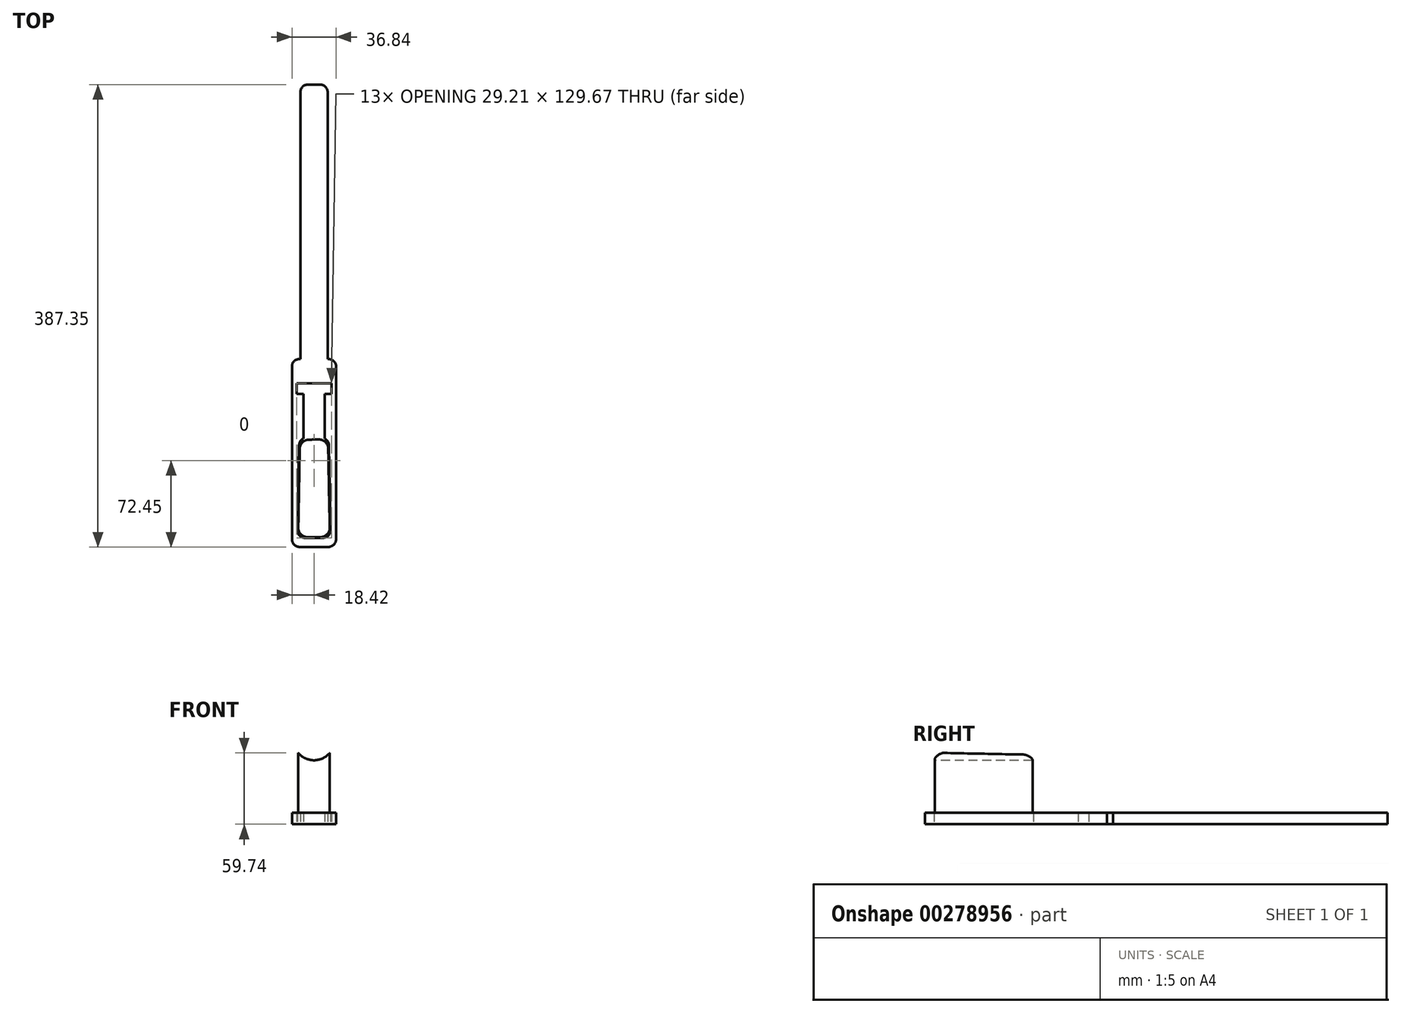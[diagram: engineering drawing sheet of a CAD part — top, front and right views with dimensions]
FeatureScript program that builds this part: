
annotation { "Feature Type Name" : "Feature", "Feature Type Description" : "" }
export const myFeature = defineFeature(function(context is Context, id is Id, definition is map)
    precondition{}
    {
        {
            var Q0;
            Q0=qCreatedBy(makeId("Top.planeOp"),FACE);
            var sketch = newSketch(context, id + "F0", { "sketchPlane" : qUnion([Q0])});
            skLineSegment(sketch, "E0", {"start": v(-18.42, 0) * mm, "end": v(-18.42, -85.1) * mm});
            skLineSegment(sketch, "E1", {"start": v(-12.07, -91.44) * mm, "end": v(12.07, -91.44) * mm});
            skLineSegment(sketch, "E2", {"start": v(18.42, -85.1) * mm, "end": v(18.42, 0) * mm});
            skLineSegment(sketch, "E3", {"start": v(-7.5, -83.82) * mm, "end": v(7.5, -83.82) * mm});
            skLineSegment(sketch, "E4", {"start": v(0, -112.75) * mm, "end": v(0, 326.55) * mm, "construction": true});
            skPoint(sketch, "E4.startSnap0", {"position": v(0, -91.44) * mm});
            skPoint(sketch, "E5", {"position": v(0, -83.82) * mm});
            skLineSegment(sketch, "E6", {"start": v(-18.42, 0) * mm, "end": v(-18.42, 60.96) * mm});
            skLineSegment(sketch, "E7", {"start": v(18.42, 0) * mm, "end": v(18.42, 60.96) * mm});
            skLineSegment(sketch, "E8", {"start": v(-8.9, 36.96) * mm, "end": v(-8.89, 0) * mm});
            skLineSegment(sketch, "E9", {"start": v(8.89, 36.96) * mm, "end": v(8.89, 0) * mm});
            skLineSegment(sketch, "E10", {"start": v(0, 0) * mm, "end": v(6.15, 0) * mm});
            skLineSegment(sketch, "E11", {"start": v(0, 0) * mm, "end": v(-6.15, 0) * mm});
            skLineSegment(sketch, "E12", {"start": v(-12.5, -6.23) * mm, "end": v(-13.85, -77.35) * mm});
            skLineSegment(sketch, "E13", {"start": v(12.5, -6.23) * mm, "end": v(13.85, -77.35) * mm});
            skPoint(sketch, "E14.visualSharp", {"position": v(-12.38, 0) * mm});
            skPoint(sketch, "E15.visualSharp", {"position": v(12.38, 0) * mm});
            skPoint(sketch, "E16.visualSharp", {"position": v(13.97, -83.82) * mm});
            skArc(sketch, "E16.filletArc", {"start": v(7.5, -83.82) * mm, "mid": v(12.03, -81.92) * mm, "end": v(13.85, -77.35) * mm});
            skPoint(sketch, "E17.visualSharp", {"position": v(-13.97, -83.82) * mm});
            skArc(sketch, "E17.filletArc", {"start": v(-13.85, -77.35) * mm, "mid": v(-12.03, -81.92) * mm, "end": v(-7.5, -83.82) * mm});
            skLineSegment(sketch, "E18", {"start": v(-8.89, 0) * mm, "end": v(-8.89, -0.62) * mm});
            skLineSegment(sketch, "E19", {"start": v(8.89, 0) * mm, "end": v(8.89, -0.62) * mm});
            skArc(sketch, "E20", {"start": v(12.5, -6.23) * mm, "mid": v(11.5, -2.91) * mm, "end": v(8.89, -0.62) * mm});
            skArc(sketch, "E21", {"start": v(-8.89, -0.62) * mm, "mid": v(-11.5, -2.91) * mm, "end": v(-12.5, -6.23) * mm});
            skLineSegment(sketch, "E22", {"start": v(0, 60.96) * mm, "end": v(11.43, 60.96) * mm});
            skLineSegment(sketch, "E23", {"start": v(0, 60.96) * mm, "end": v(-11.43, 60.96) * mm});
            skPoint(sketch, "E24", {"position": v(-18.42, 54.6) * mm});
            skPoint(sketch, "E25", {"position": v(18.42, 54.6) * mm});
            skLineSegment(sketch, "E26", {"start": v(-11.43, 60.96) * mm, "end": v(-11.43, 289.56) * mm});
            skLineSegment(sketch, "E27", {"start": v(-5.08, 295.91) * mm, "end": v(5.08, 295.91) * mm});
            skLineSegment(sketch, "E28", {"start": v(11.43, 289.56) * mm, "end": v(11.43, 60.96) * mm});
            skLineSegment(sketch, "E29", {"start": v(0, 60.96) * mm, "end": v(-12.07, 60.96) * mm});
            skLineSegment(sketch, "E30", {"start": v(0, 60.96) * mm, "end": v(12.07, 60.96) * mm});
            skArc(sketch, "E31", {"start": v(-12.07, 60.96) * mm, "mid": v(-16.56, 59.1) * mm, "end": v(-18.42, 54.6) * mm});
            skArc(sketch, "E32", {"start": v(18.42, 54.6) * mm, "mid": v(16.56, 59.1) * mm, "end": v(12.07, 60.96) * mm});
            skPoint(sketch, "E33.visualSharp", {"position": v(-11.43, 289.56) * mm});
            skArc(sketch, "E33.filletArc", {"start": v(-5.08, 295.91) * mm, "mid": v(-9.57, 294.05) * mm, "end": v(-11.43, 289.56) * mm});
            skPoint(sketch, "E34.visualSharp", {"position": v(11.43, 289.56) * mm});
            skArc(sketch, "E34.filletArc", {"start": v(11.43, 289.56) * mm, "mid": v(9.57, 294.05) * mm, "end": v(5.08, 295.91) * mm});
            skLineSegment(sketch, "E35", {"start": v(8.89, 36.96) * mm, "end": v(14.6, 36.96) * mm});
            skLineSegment(sketch, "E36", {"start": v(-8.9, 36.96) * mm, "end": v(-14.6, 36.96) * mm});
            skPoint(sketch, "E37.visualSharp", {"position": v(-18.42, -91.44) * mm});
            skArc(sketch, "E37.filletArc", {"start": v(-18.41, -85.1) * mm, "mid": v(-16.56, -89.58) * mm, "end": v(-12.07, -91.44) * mm});
            skPoint(sketch, "E38.visualSharp", {"position": v(18.42, -91.44) * mm});
            skArc(sketch, "E38.filletArc", {"start": v(12.07, -91.44) * mm, "mid": v(16.56, -89.58) * mm, "end": v(18.41, -85.1) * mm});
            skLineSegment(sketch, "E39", {"start": v(12.07, 66.04) * mm, "end": v(-12.07, 66.04) * mm});
            skArc(sketch, "E40", {"start": v(-12.07, 66.04) * mm, "mid": v(-16.13, 64.61) * mm, "end": v(-18.42, 60.96) * mm});
            skArc(sketch, "E41", {"start": v(18.42, 60.96) * mm, "mid": v(16.13, 64.61) * mm, "end": v(12.07, 66.04) * mm});
            skPoint(sketch, "E42", {"position": v(14.6, 45.85) * mm});
            skLineSegment(sketch, "E43", {"start": v(14.6, 36.96) * mm, "end": v(14.6, 45.85) * mm});
            skLineSegment(sketch, "E44", {"start": v(-14.6, 45.85) * mm, "end": v(-14.6, 36.96) * mm});
            skLineSegment(sketch, "E45", {"start": v(-14.6, 45.85) * mm, "end": v(14.6, 45.85) * mm});
            skSolve(sketch);
        }
        {
            var Q0;
            Q0 = qSketchRegion(id + "F0", true);
            extrude(context, id + "F1", {"entities" : qUnion([Q0]), "depth" : 9.52 * mm});
        }
        {
            var Q0;
            Q0=makeQuery(id+"F1.opExtrude","SWEPT_BODY",BODY,{"disambiguationData":[OSD([sQuery(id+"F0.wireOp",EDGE,"E0"),sQuery(id+"F0.wireOp",EDGE,"E1"),sQuery(id+"F0.wireOp",EDGE,"E2"),sQuery(id+"F0.wireOp",EDGE,"E3"),sQuery(id+"F0.wireOp",EDGE,"E6"),sQuery(id+"F0.wireOp",EDGE,"E7"),sQuery(id+"F0.wireOp",EDGE,"E8"),sQuery(id+"F0.wireOp",EDGE,"E9"),sQuery(id+"F0.wireOp",EDGE,"E12"),sQuery(id+"F0.wireOp",EDGE,"E13"),sQuery(id+"F0.wireOp",EDGE,"E16.filletArc"),sQuery(id+"F0.wireOp",EDGE,"E17.filletArc"),sQuery(id+"F0.wireOp",EDGE,"E18"),sQuery(id+"F0.wireOp",EDGE,"E19"),sQuery(id+"F0.wireOp",EDGE,"E20"),sQuery(id+"F0.wireOp",EDGE,"E21"),sQuery(id+"F0.wireOp",EDGE,"06W7z1AY-n0ql-A3Bi-P6vR-q7lxeoe17qw5"),sQuery(id+"F0.wireOp",EDGE,"bXarmPJa-DHQA-tuoh-5tIz-POXl1eP8OdJ6"),sQuery(id+"F0.wireOp",EDGE,"ymd9te90-yEeZ-0O9O-FOdn-OmkhNjDWxyUQ"),sQuery(id+"F0.wireOp",EDGE,"E26"),sQuery(id+"F0.wireOp",EDGE,"E27"),sQuery(id+"F0.wireOp",EDGE,"E28"),sQuery(id+"F0.wireOp",EDGE,"E33.filletArc"),sQuery(id+"F0.wireOp",EDGE,"E34.filletArc"),sQuery(id+"F0.wireOp",EDGE,"E35"),sQuery(id+"F0.wireOp",EDGE,"E36"),sQuery(id+"F0.wireOp",EDGE,"E37.filletArc"),sQuery(id+"F0.wireOp",EDGE,"E38.filletArc"),sQuery(id+"F0.wireOp",EDGE,"E39"),sQuery(id+"F0.wireOp",EDGE,"E40"),sQuery(id+"F0.wireOp",EDGE,"E41")])]});
            transform(context, id + "F2", {"entities" : qUnion([Q0]), "transformType" : TransformType.TRANSLATION_3D, "dx" : 0 * mm, "dy" : -113.28 * mm, "dz" : 0 * mm, "makeCopy" : false});
        }
        {
            var Q0;
            Q0=makeQuery(id+"F1.opExtrude","CAP_FACE",FACE,{"disambiguationData":[OSD([sQuery(id+"F0.wireOp",EDGE,"E0"),sQuery(id+"F0.wireOp",EDGE,"E1"),sQuery(id+"F0.wireOp",EDGE,"E2"),sQuery(id+"F0.wireOp",EDGE,"E3"),sQuery(id+"F0.wireOp",EDGE,"E6"),sQuery(id+"F0.wireOp",EDGE,"E7"),sQuery(id+"F0.wireOp",EDGE,"E8"),sQuery(id+"F0.wireOp",EDGE,"E9"),sQuery(id+"F0.wireOp",EDGE,"E12"),sQuery(id+"F0.wireOp",EDGE,"E13"),sQuery(id+"F0.wireOp",EDGE,"E16.filletArc"),sQuery(id+"F0.wireOp",EDGE,"E17.filletArc"),sQuery(id+"F0.wireOp",EDGE,"E18"),sQuery(id+"F0.wireOp",EDGE,"E19"),sQuery(id+"F0.wireOp",EDGE,"E20"),sQuery(id+"F0.wireOp",EDGE,"E21"),sQuery(id+"F0.wireOp",EDGE,"E26"),sQuery(id+"F0.wireOp",EDGE,"E27"),sQuery(id+"F0.wireOp",EDGE,"E28"),sQuery(id+"F0.wireOp",EDGE,"E33.filletArc"),sQuery(id+"F0.wireOp",EDGE,"E34.filletArc"),sQuery(id+"F0.wireOp",EDGE,"E35"),sQuery(id+"F0.wireOp",EDGE,"E36"),sQuery(id+"F0.wireOp",EDGE,"E37.filletArc"),sQuery(id+"F0.wireOp",EDGE,"E38.filletArc"),sQuery(id+"F0.wireOp",EDGE,"E39"),sQuery(id+"F0.wireOp",EDGE,"E40"),sQuery(id+"F0.wireOp",EDGE,"E41"),sQuery(id+"F0.wireOp",EDGE,"E43"),sQuery(id+"F0.wireOp",EDGE,"E44"),sQuery(id+"F0.wireOp",EDGE,"E45")])],"isStart":false});
            var sketch = newSketch(context, id + "F3", { "sketchPlane" : qUnion([Q0])});
            skArc(sketch, "E46", {"start": v(-12.07, -47.24) * mm, "mid": v(-16.13, -48.67) * mm, "end": v(-18.42, -52.32) * mm});
            skArc(sketch, "E47", {"start": v(18.42, -52.32) * mm, "mid": v(16.13, -48.67) * mm, "end": v(12.07, -47.24) * mm});
            skArc(sketch, "E48", {"start": v(12.07, -204.72) * mm, "mid": v(16.56, -202.86) * mm, "end": v(18.41, -198.37) * mm});
            skArc(sketch, "E49", {"start": v(7.5, -197.1) * mm, "mid": v(12.03, -195.2) * mm, "end": v(13.85, -190.63) * mm});
            skArc(sketch, "E50", {"start": v(-13.85, -190.63) * mm, "mid": v(-12.03, -195.2) * mm, "end": v(-7.5, -197.1) * mm});
            skArc(sketch, "E51", {"start": v(-18.41, -198.37) * mm, "mid": v(-16.56, -202.86) * mm, "end": v(-12.07, -204.72) * mm});
            skArc(sketch, "E52", {"start": v(-8.89, -113.9) * mm, "mid": v(-11.5, -116.2) * mm, "end": v(-12.5, -119.51) * mm});
            skArc(sketch, "E53", {"start": v(12.5, -119.51) * mm, "mid": v(11.5, -116.2) * mm, "end": v(8.89, -113.9) * mm});
            skArc(sketch, "E54", {"start": v(-5.08, 182.63) * mm, "mid": v(-9.57, 180.77) * mm, "end": v(-11.43, 176.28) * mm});
            skArc(sketch, "E55", {"start": v(11.43, 176.28) * mm, "mid": v(9.57, 180.77) * mm, "end": v(5.08, 182.63) * mm});
            skLineSegment(sketch, "E56", {"start": v(-5.08, 182.63) * mm, "end": v(5.08, 182.63) * mm});
            skLineSegment(sketch, "E57", {"start": v(-12.07, -47.24) * mm, "end": v(-11.43, -47.24) * mm});
            skLineSegment(sketch, "E58", {"start": v(-11.43, -47.24) * mm, "end": v(-11.43, 176.28) * mm});
            skLineSegment(sketch, "E59", {"start": v(11.43, 176.28) * mm, "end": v(11.43, -47.24) * mm});
            skLineSegment(sketch, "E60", {"start": v(11.43, -47.24) * mm, "end": v(12.07, -47.24) * mm});
            skLineSegment(sketch, "E61", {"start": v(-8.89, -113.9) * mm, "end": v(-8.89, -76.33) * mm});
            skLineSegment(sketch, "E62", {"start": v(-8.89, -76.33) * mm, "end": v(-14.6, -76.33) * mm});
            skLineSegment(sketch, "E63", {"start": v(-14.6, -76.33) * mm, "end": v(-14.6, -67.44) * mm});
            skLineSegment(sketch, "E64", {"start": v(-14.6, -67.44) * mm, "end": v(14.6, -67.44) * mm});
            skLineSegment(sketch, "E65", {"start": v(14.6, -67.44) * mm, "end": v(14.6, -76.33) * mm});
            skLineSegment(sketch, "E66", {"start": v(14.6, -76.33) * mm, "end": v(8.89, -76.33) * mm});
            skLineSegment(sketch, "E67", {"start": v(8.89, -76.33) * mm, "end": v(8.89, -113.9) * mm});
            skLineSegment(sketch, "E68", {"start": v(-13.85, -190.63) * mm, "end": v(-12.5, -119.51) * mm});
            skLineSegment(sketch, "E69", {"start": v(12.5, -119.51) * mm, "end": v(13.85, -190.63) * mm});
            skLineSegment(sketch, "E70", {"start": v(7.5, -197.1) * mm, "end": v(-7.5, -197.1) * mm});
            skLineSegment(sketch, "E71", {"start": v(-12.07, -204.72) * mm, "end": v(12.07, -204.72) * mm});
            skLineSegment(sketch, "E72", {"start": v(-18.42, -52.32) * mm, "end": v(-18.41, -198.37) * mm});
            skLineSegment(sketch, "E73", {"start": v(18.41, -198.37) * mm, "end": v(18.42, -52.32) * mm});
            skSolve(sketch);
        }
        {
            var Q0;
            Q0=makeQuery(id+"F3.imprint","IMPRINT",FACE,{"disambiguationData":[TD([[makeQuery(id+"F3.imprint","IMPRINT",EDGE,{"derivedFrom":sQuery(id+"F3.wireOp",EDGE,"E46")}),1.0]])]});
            var sketch = newSketch(context, id + "F4", { "sketchPlane" : qUnion([Q0])});
            skLineSegment(sketch, "E74", {"start": v(-5.43, -197.1) * mm, "end": v(5.43, -197.1) * mm, "construction": true});
            skLineSegment(sketch, "E75", {"start": v(13.8, -188.56) * mm, "end": v(12.55, -122.22) * mm, "construction": true});
            skLineSegment(sketch, "E76", {"start": v(4.01, -114) * mm, "end": v(-4.33, -114.16) * mm, "construction": true});
            skLineSegment(sketch, "E77", {"start": v(-12.55, -122.38) * mm, "end": v(-13.8, -188.56) * mm, "construction": true});
            skPoint(sketch, "E78.visualSharp", {"position": v(-13.97, -197.1) * mm});
            skArc(sketch, "E78.filletArc", {"start": v(-13.8, -188.56) * mm, "mid": v(-11.41, -194.6) * mm, "end": v(-5.43, -197.1) * mm, "construction": true});
            skPoint(sketch, "E79.visualSharp", {"position": v(13.97, -197.1) * mm});
            skArc(sketch, "E79.filletArc", {"start": v(5.43, -197.1) * mm, "mid": v(11.41, -194.6) * mm, "end": v(13.8, -188.56) * mm, "construction": true});
            skPoint(sketch, "E80.visualSharp", {"position": v(-12.4, -114.3) * mm});
            skArc(sketch, "E80.filletArc", {"start": v(-4.33, -114.16) * mm, "mid": v(-10.1, -116.6) * mm, "end": v(-12.55, -122.38) * mm, "construction": true});
            skPoint(sketch, "E81.visualSharp", {"position": v(12.4, -113.84) * mm});
            skArc(sketch, "E81.filletArc", {"start": v(12.55, -122.22) * mm, "mid": v(9.98, -116.34) * mm, "end": v(4.01, -114) * mm, "construction": true});
            skLineSegment(sketch, "E82.0", {"start": v(-11.92, -122.39) * mm, "end": v(-13.17, -188.58) * mm});
            skArc(sketch, "E82.1", {"start": v(-4.32, -114.8) * mm, "mid": v(-9.65, -117.06) * mm, "end": v(-11.92, -122.39) * mm});
            skArc(sketch, "E82.2", {"start": v(-13.17, -188.58) * mm, "mid": v(-10.96, -194.15) * mm, "end": v(-5.43, -196.47) * mm});
            skLineSegment(sketch, "E82.3", {"start": v(4.02, -114.63) * mm, "end": v(-4.32, -114.8) * mm});
            skLineSegment(sketch, "E82.4", {"start": v(-5.43, -196.47) * mm, "end": v(5.43, -196.47) * mm});
            skArc(sketch, "E82.5", {"start": v(5.43, -196.47) * mm, "mid": v(10.96, -194.15) * mm, "end": v(13.17, -188.58) * mm});
            skLineSegment(sketch, "E82.6", {"start": v(13.17, -188.58) * mm, "end": v(11.92, -122.23) * mm});
            skArc(sketch, "E82.7", {"start": v(11.92, -122.23) * mm, "mid": v(9.54, -116.8) * mm, "end": v(4.02, -114.63) * mm});
            skSolve(sketch);
        }
        {
            var Q0;
            Q0=makeQuery(id+"F4.imprint","IMPRINT",FACE,{"disambiguationData":[TD([[makeQuery(id+"F4.imprint","IMPRINT",EDGE,{"derivedFrom":sQuery(id+"F4.wireOp",EDGE,"E82.0")}),1.0]])]});
            extrude(context, id + "F5", {"entities" : qUnion([Q0]), "depth" : 50.8 * mm});
        }
        {
            var Q0;
            Q0=makeQuery(id+"F5.opExtrude","SWEPT_FACE",FACE,{"disambiguationData":[OSD([sQuery(id+"F4.wireOp",EDGE,"E82.4")])]});
            var sketch = newSketch(context, id + "F6", { "sketchPlane" : qUnion([Q0])});
            skCircle(sketch, "E83", {"center": v(0, 70.77) * mm, "radius": 17.18 * mm});
            skPoint(sketch, "E83.centerSnap0", {"position": v(0, 60.33) * mm});
            skSolve(sketch);
        }
        {
            var Q0;
            Q0 = qSketchRegion(id + "F6", true);
            var Q1;
            Q1=makeQuery(id+"F5.opExtrude","SWEPT_FACE",FACE,{"disambiguationData":[OSD([sQuery(id+"F4.wireOp",EDGE,"E82.3")])]});
            extrude(context, id + "F7", {"entities" : qUnion([Q0]), "operationType" : NewBodyOperationType.REMOVE, "endBound" : BoundingType.UP_TO_SURFACE, "oppositeDirection" : true, "endBoundEntityFace" : qUnion([Q1]), "depth" : 25.4 * mm});
        }
    });
